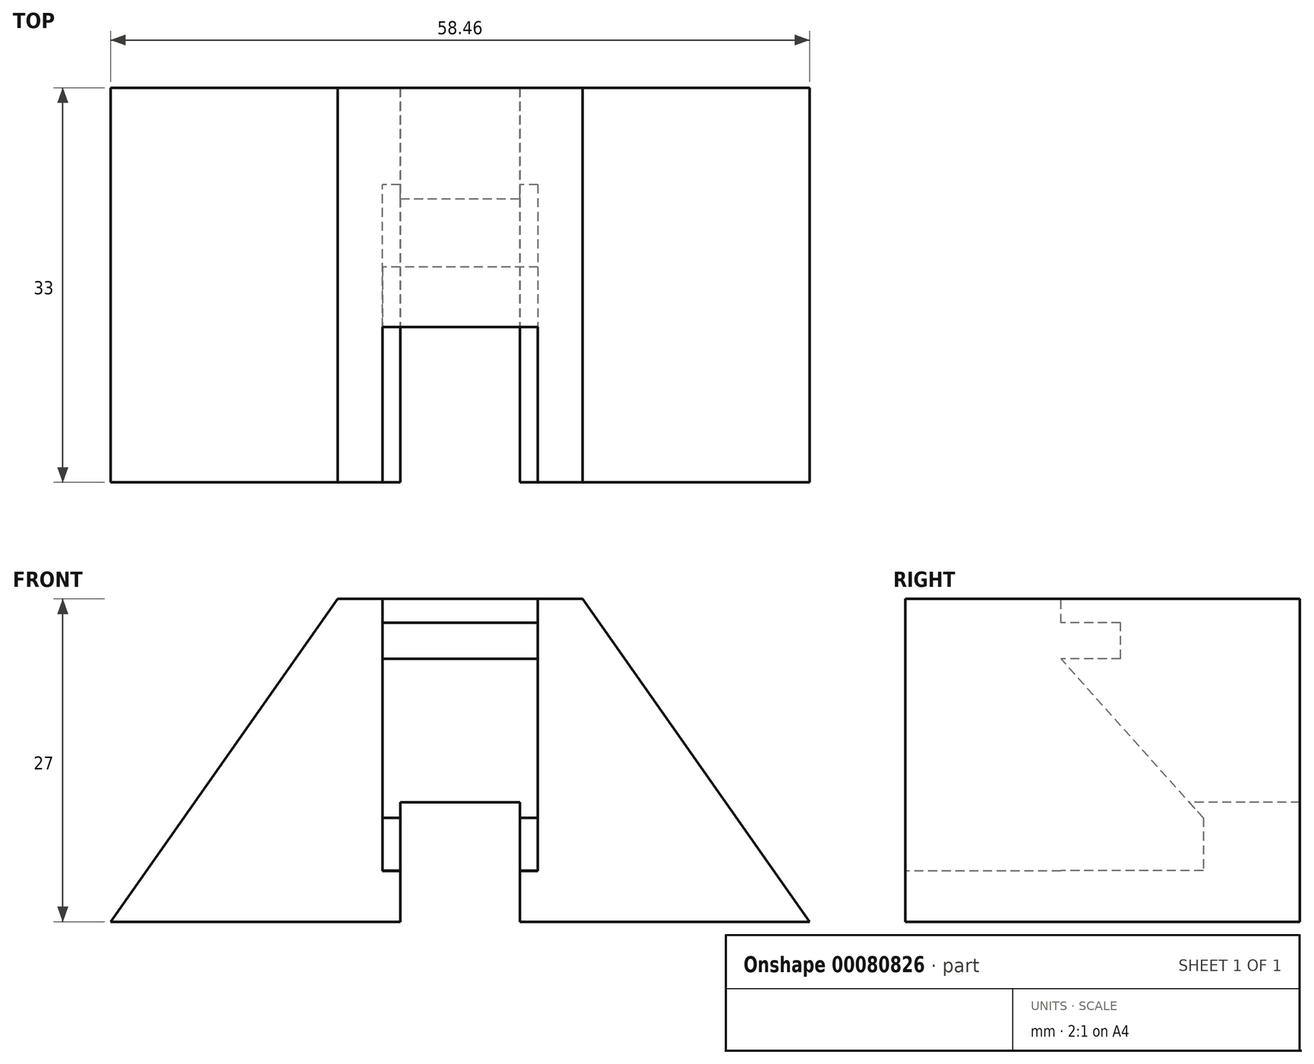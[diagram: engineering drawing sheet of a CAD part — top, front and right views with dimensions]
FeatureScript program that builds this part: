
annotation { "Feature Type Name" : "Feature", "Feature Type Description" : "" }
export const myFeature = defineFeature(function(context is Context, id is Id, definition is map)
    precondition{}
    {
        {
            var Q0;
            Q0=qCreatedBy(makeId("Top.planeOp"),FACE);
            var sketch = newSketch(context, id + "F0", { "sketchPlane" : qUnion([Q0])});
            skLineSegment(sketch, "E0.bottom", {"start": v(29.23, 16.5) * mm, "end": v(-29.22, 16.5) * mm});
            skLineSegment(sketch, "E0.top", {"start": v(29.23, -16.5) * mm, "end": v(-29.23, -16.5) * mm});
            skLineSegment(sketch, "E0.left", {"start": v(29.23, 16.5) * mm, "end": v(29.23, -16.5) * mm});
            skLineSegment(sketch, "E0.right", {"start": v(-29.22, 16.5) * mm, "end": v(-29.23, -16.5) * mm});
            skPoint(sketch, "E0.middle", {"position": v(0, 0) * mm});
            skSolve(sketch);
        }
        {
            var Q0;
            Q0 = qSketchRegion(id + "F0", true);
            extrude(context, id + "F1", {"entities" : qUnion([Q0]), "depth" : 27 * mm});
        }
        {
            var Q0;
            Q0=makeQuery(id+"F1.opExtrude","SWEPT_FACE",FACE,{"disambiguationData":[OSD([sQuery(id+"F0.wireOp",EDGE,"E0.top")])]});
            var sketch = newSketch(context, id + "F2", { "sketchPlane" : qUnion([Q0])});
            skLineSegment(sketch, "E1", {"start": v(-29.23, 0) * mm, "end": v(-10.25, 27) * mm});
            skLineSegment(sketch, "E2", {"start": v(-10.25, 27) * mm, "end": v(-10.25, 0) * mm});
            skLineSegment(sketch, "E3", {"start": v(-10.25, 0) * mm, "end": v(-29.23, 0) * mm});
            skLineSegment(sketch, "E4", {"start": v(29.23, 0) * mm, "end": v(10.25, 27) * mm});
            skLineSegment(sketch, "E5", {"start": v(10.25, 27) * mm, "end": v(10.25, 0) * mm});
            skLineSegment(sketch, "E6", {"start": v(10.25, 0) * mm, "end": v(29.23, 0) * mm});
            skSolve(sketch);
        }
        {
            var Q0;
            {var subQ0=sQuery(id+"F2.wireOp",EDGE,"E1");Q0=makeQuery(id+"F2.imprint","IMPRINT",FACE,{"disambiguationData":[TD([[makeQuery(id+"F2.imprint","IMPRINT",EDGE,{"derivedFrom":subQ0}),1.0]])]});}
            var Q1;
            {var subQ0=sQuery(id+"F2.wireOp",EDGE,"E4");Q1=makeQuery(id+"F2.imprint","IMPRINT",FACE,{"disambiguationData":[TD([[makeQuery(id+"F2.imprint","IMPRINT",EDGE,{"derivedFrom":subQ0}),-1.0]])]});}
            extrude(context, id + "F3", {"entities" : qUnion([Q0, Q1]), "operationType" : NewBodyOperationType.REMOVE, "oppositeDirection" : true, "depth" : 33 * mm});
        }
        {
            var Q0;
            Q0=makeQuery(id+"F1.opExtrude","CAP_FACE",FACE,{"disambiguationData":[OSD([sQuery(id+"F0.wireOp",EDGE,"E0.bottom"),sQuery(id+"F0.wireOp",EDGE,"E0.top"),sQuery(id+"F0.wireOp",EDGE,"E0.left"),sQuery(id+"F0.wireOp",EDGE,"E0.right")])],"isStart":false});
            var sketch = newSketch(context, id + "F4", { "sketchPlane" : qUnion([Q0])});
            skLineSegment(sketch, "E7.bottom", {"start": v(5, -16.5) * mm, "end": v(-5, -16.5) * mm});
            skLineSegment(sketch, "E7.top", {"start": v(5, -3.5) * mm, "end": v(-5, -3.5) * mm});
            skLineSegment(sketch, "E7.left", {"start": v(5, -16.5) * mm, "end": v(5, -3.5) * mm});
            skLineSegment(sketch, "E7.right", {"start": v(-5, -16.5) * mm, "end": v(-5, -3.5) * mm});
            skPoint(sketch, "E7.middle", {"position": v(0, -10) * mm});
            skSolve(sketch);
        }
        {
            var Q0;
            Q0 = qSketchRegion(id + "F4", true);
            extrude(context, id + "F5", {"entities" : qUnion([Q0]), "operationType" : NewBodyOperationType.REMOVE, "oppositeDirection" : true, "depth" : 27 * mm});
        }
        {
            var Q0;
            Q0=makeQuery(id+"F1.opExtrude","CAP_FACE",FACE,{"disambiguationData":[OSD([sQuery(id+"F0.wireOp",EDGE,"E0.bottom"),sQuery(id+"F0.wireOp",EDGE,"E0.top"),sQuery(id+"F0.wireOp",EDGE,"E0.left"),sQuery(id+"F0.wireOp",EDGE,"E0.right")])],"isStart":false});
            var sketch = newSketch(context, id + "F6", { "sketchPlane" : qUnion([Q0])});
            skLineSegment(sketch, "E8.bottom", {"start": v(6.5, -16.5) * mm, "end": v(-6.5, -16.5) * mm});
            skLineSegment(sketch, "E8.top", {"start": v(6.5, -3.5) * mm, "end": v(-6.5, -3.5) * mm});
            skLineSegment(sketch, "E8.left", {"start": v(6.5, -16.5) * mm, "end": v(6.5, -3.5) * mm});
            skLineSegment(sketch, "E8.right", {"start": v(-6.5, -16.5) * mm, "end": v(-6.5, -3.5) * mm});
            skPoint(sketch, "E8.middle", {"position": v(0, -10) * mm});
            skPoint(sketch, "E8.middle.positionSnap0", {"position": v(5, -10) * mm});
            skPoint(sketch, "E8.middle.positionSnap1", {"position": v(0, -3.5) * mm});
            skPoint(sketch, "E8.centerSnap0", {"position": v(5, -10) * mm});
            skPoint(sketch, "E8.centerSnap1", {"position": v(0, -3.5) * mm});
            skSolve(sketch);
        }
        {
            var Q0;
            Q0 = qSketchRegion(id + "F6", true);
            extrude(context, id + "F7", {"entities" : qUnion([Q0]), "operationType" : NewBodyOperationType.REMOVE, "oppositeDirection" : true, "depth" : 22.75 * mm});
        }
        {
            var Q0;
            Q0=makeQuery(id+"F7.boolean.opBoolean","MERGE",FACE,{"derivedFrom":[makeQuery(id+"F5.boolean.opBoolean","COPY",FACE,{"derivedFrom":makeQuery(id+"F5.opExtrude","SWEPT_FACE",FACE,{"disambiguationData":[OSD([sQuery(id+"F4.wireOp",EDGE,"E7.top")])]})}),makeQuery(id+"F7.opExtrude","SWEPT_FACE",FACE,{"disambiguationData":[OSD([sQuery(id+"F6.wireOp",EDGE,"E8.top")])]})]});
            var sketch = newSketch(context, id + "F8", { "sketchPlane" : qUnion([Q0])});
            skLineSegment(sketch, "E9.bottom", {"start": v(6.5, 22) * mm, "end": v(-6.5, 22) * mm});
            skLineSegment(sketch, "E9.top", {"start": v(6.5, 25) * mm, "end": v(-6.5, 25) * mm});
            skLineSegment(sketch, "E9.left", {"start": v(6.5, 22) * mm, "end": v(6.5, 25) * mm});
            skLineSegment(sketch, "E9.right", {"start": v(-6.5, 22) * mm, "end": v(-6.5, 25) * mm});
            skPoint(sketch, "E9.middle", {"position": v(0, 23.5) * mm});
            skSolve(sketch);
        }
        {
            var Q0;
            Q0 = qSketchRegion(id + "F8", true);
            extrude(context, id + "F9", {"entities" : qUnion([Q0]), "operationType" : NewBodyOperationType.REMOVE, "oppositeDirection" : true, "depth" : 5 * mm});
        }
        {
            var Q0;
            {var subQ2=sQuery(id+"F6.wireOp",EDGE,"E8.top");Q0=makeQuery(id+"F9.boolean.opBoolean","SPLIT",FACE,{"disambiguationData":[TD([makeQuery(id+"F5.boolean.opBoolean","COPY",FACE,{"derivedFrom":makeQuery(id+"F5.opExtrude","SWEPT_FACE",FACE,{"disambiguationData":[OSD([sQuery(id+"F4.wireOp",EDGE,"E7.left")])]})})])],"derivedFrom":makeQuery(id+"F7.boolean.opBoolean","MERGE",FACE,{"derivedFrom":[makeQuery(id+"F5.boolean.opBoolean","COPY",FACE,{"derivedFrom":makeQuery(id+"F5.opExtrude","SWEPT_FACE",FACE,{"disambiguationData":[OSD([sQuery(id+"F4.wireOp",EDGE,"E7.top")])]})}),makeQuery(id+"F7.opExtrude","SWEPT_FACE",FACE,{"disambiguationData":[OSD([subQ2])]})]})});}
            var sketch = newSketch(context, id + "F10", { "sketchPlane" : qUnion([Q0])});
            skLineSegment(sketch, "E10.bottom", {"start": v(5, 0) * mm, "end": v(-5, 0) * mm});
            skLineSegment(sketch, "E10.top", {"start": v(5, 10) * mm, "end": v(-5, 10) * mm});
            skLineSegment(sketch, "E10.left", {"start": v(5, 0) * mm, "end": v(5, 10) * mm});
            skLineSegment(sketch, "E10.right", {"start": v(-5, 0) * mm, "end": v(-5, 10) * mm});
            skPoint(sketch, "E10.middle", {"position": v(0, 5) * mm});
            skSolve(sketch);
        }
        {
            var Q0;
            Q0 = qSketchRegion(id + "F10", true);
            extrude(context, id + "F11", {"entities" : qUnion([Q0]), "operationType" : NewBodyOperationType.REMOVE, "oppositeDirection" : true, "depth" : 33 * mm});
        }
        {
            var Q0;
            Q0=qCreatedBy(makeId("Right.planeOp"),FACE);
            var sketch = newSketch(context, id + "F12", { "sketchPlane" : qUnion([Q0])});
            skLineSegment(sketch, "E11", {"start": v(-3.5, 4.26) * mm, "end": v(8.41, 4.26) * mm});
            skLineSegment(sketch, "E12", {"start": v(8.41, 4.26) * mm, "end": v(8.41, 8.68) * mm});
            skLineSegment(sketch, "E13", {"start": v(8.41, 8.68) * mm, "end": v(-3.5, 22) * mm});
            skLineSegment(sketch, "E14", {"start": v(-3.5, 22) * mm, "end": v(-3.5, 4.26) * mm});
            skLineSegment(sketch, "E15", {"start": v(-3.5, 22) * mm, "end": v(48.87, 22) * mm, "construction": true});
            skSolve(sketch);
        }
        {
            var Q0;
            Q0 = qSketchRegion(id + "F12", true);
            extrude(context, id + "F13", {"entities" : qUnion([Q0]), "operationType" : NewBodyOperationType.REMOVE, "endBound" : BoundingType.SYMMETRIC, "depth" : 13 * mm});
        }
    });
